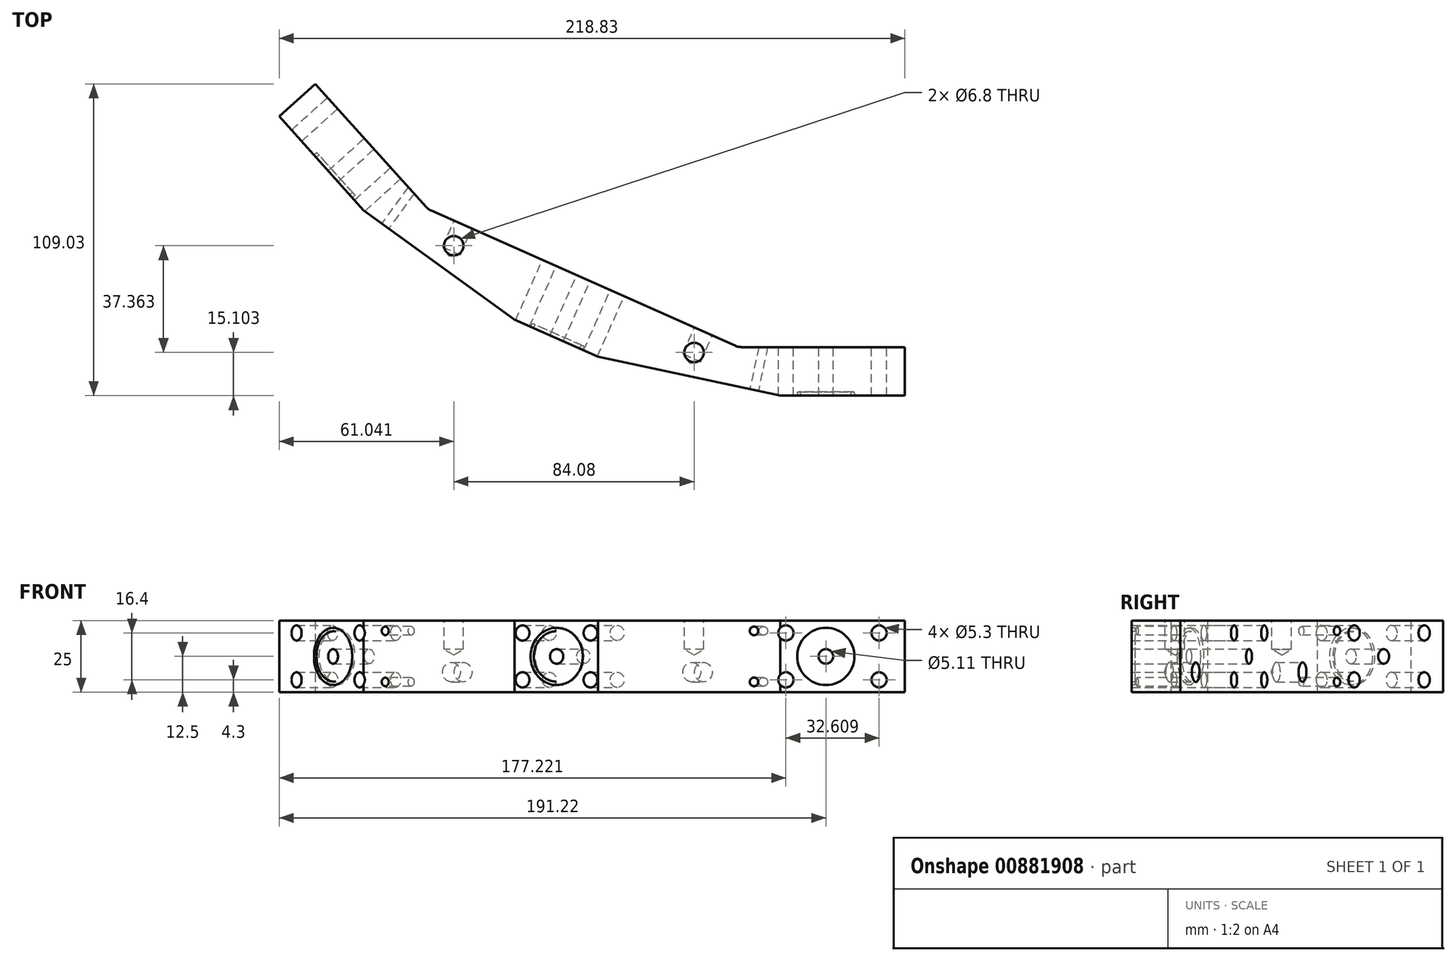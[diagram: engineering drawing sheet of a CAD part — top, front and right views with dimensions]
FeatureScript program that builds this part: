
annotation { "Feature Type Name" : "Feature", "Feature Type Description" : "" }
export const myFeature = defineFeature(function(context is Context, id is Id, definition is map)
    precondition{}
    {
        {
            var Q0;
            Q0=qCreatedBy(makeId("Top.planeOp"),FACE);
            var sketch = newSketch(context, id + "F0", { "sketchPlane" : qUnion([Q0])});
            skCircle(sketch, "E0", {"center": v(0, -260) * mm, "radius": 6 * mm});
            skCircle(sketch, "E1", {"center": v(-105.75, -237.52) * mm, "radius": 6 * mm});
            skCircle(sketch, "E2", {"center": v(-193.22, -173.97) * mm, "radius": 6 * mm});
            skPoint(sketch, "E3", {"position": v(-185.79, -167.28) * mm});
            skPoint(sketch, "E4", {"position": v(-101.68, -228.39) * mm});
            skPoint(sketch, "E5", {"position": v(0, -250) * mm});
            skLineSegment(sketch, "E6.trimOffspring", {"start": v(-103.31, -232.04) * mm, "end": v(-105.75, -237.52) * mm});
            skLineSegment(sketch, "E7.trimOffspring", {"start": v(0, -254) * mm, "end": v(0, -260) * mm});
            skLineSegment(sketch, "E8.trimOffspring", {"start": v(-188.76, -169.96) * mm, "end": v(-193.22, -173.97) * mm});
            skPoint(sketch, "E9", {"position": v(-196.5, -155.4) * mm});
            skPoint(sketch, "E10", {"position": v(-94.36, -211.94) * mm});
            skLineSegment(sketch, "E11", {"start": v(-161.7, -167.13) * mm, "end": v(-108.98, -205.43) * mm});
            skPoint(sketch, "E12", {"position": v(0, -232) * mm});
            skLineSegment(sketch, "E13", {"start": v(0, -232) * mm, "end": v(27.61, -232) * mm});
            skLineSegment(sketch, "E14", {"start": v(0, -232) * mm, "end": v(-16, -232) * mm});
            skLineSegment(sketch, "E15", {"start": v(-79.7, -218.33) * mm, "end": v(-16, -232) * mm});
            skPoint(sketch, "E16.start.orphan", {"position": v(0, 0) * mm});
            skPoint(sketch, "E17.visualSharp", {"position": v(16, -250) * mm});
            skLineSegment(sketch, "E18", {"start": v(-191.22, -134.35) * mm, "end": v(-178.58, -122.97) * mm});
            skLineSegment(sketch, "E19", {"start": v(27.61, -232) * mm, "end": v(27.61, -215) * mm});
            skLineSegment(sketch, "E20", {"start": v(-178.58, -122.97) * mm, "end": v(-149.07, -155.75) * mm});
            skLineSegment(sketch, "E21", {"start": v(-191.22, -134.35) * mm, "end": v(-161.7, -167.13) * mm});
            skLineSegment(sketch, "E22", {"start": v(-16, -215) * mm, "end": v(27.61, -215) * mm});
            skLineSegment(sketch, "E23", {"start": v(-108.98, -205.43) * mm, "end": v(-79.7, -218.33) * mm});
            skLineSegment(sketch, "E24", {"start": v(-125.57, -172.83) * mm, "end": v(-44.45, -208.87) * mm});
            skPoint(sketch, "E25.orphan", {"position": v(-102.07, -189.9) * mm});
            skPoint(sketch, "E26.orphan", {"position": v(-72.9, -202.75) * mm});
            skLineSegment(sketch, "E27", {"start": v(-125.57, -172.83) * mm, "end": v(-138.14, -167.24) * mm});
            skLineSegment(sketch, "E28", {"start": v(-149.07, -155.75) * mm, "end": v(-139.83, -166.02) * mm});
            skLineSegment(sketch, "E29", {"start": v(-44.45, -208.87) * mm, "end": v(-31.64, -214.57) * mm});
            skLineSegment(sketch, "E30", {"start": v(-16, -215) * mm, "end": v(-29.6, -215) * mm});
            skPoint(sketch, "E31.visualSharp", {"position": v(-139.12, -166.8) * mm});
            skArc(sketch, "E31.filletArc", {"start": v(-139.83, -166.02) * mm, "mid": v(-139.05, -166.72) * mm, "end": v(-138.14, -167.24) * mm});
            skPoint(sketch, "E32.visualSharp", {"position": v(-30.67, -215) * mm});
            skArc(sketch, "E32.filletArc", {"start": v(-31.64, -214.57) * mm, "mid": v(-30.65, -214.9) * mm, "end": v(-29.6, -215) * mm});
            skSolve(sketch);
        }
        {
            var Q0;
            Q0=makeQuery(id+"F0.imprint","IMPRINT",FACE,{"disambiguationData":[TD([[makeQuery(id+"F0.imprint","IMPRINT",EDGE,{"derivedFrom":sQuery(id+"F0.wireOp",EDGE,"E11")}),1.0]])]});
            extrude(context, id + "F1", {"entities" : qUnion([Q0]), "depth" : 25 * mm, "offsetDistance" : 25 * mm});
        }
        {
            var Q0;
            Q0=makeQuery(id+"F1.opExtrude","SWEPT_FACE",FACE,{"disambiguationData":[OSD([sQuery(id+"F0.wireOp",EDGE,"E22")])]});
            var sketch = newSketch(context, id + "F2", { "sketchPlane" : qUnion([Q0])});
            skPoint(sketch, "E33", {"position": v(0, 0) * mm});
            skLineSegment(sketch, "E34", {"start": v(0, 0) * mm, "end": v(0, 25) * mm});
            skPoint(sketch, "E35", {"position": v(0, 12.5) * mm});
            skSolve(sketch);
        }
        {
            var Q0;
            Q0=sQuery(id+"F2.wireOp",VERTEX,"E35");
            var Q1;
            Q1=makeQuery(id+"F1.opExtrude","SWEPT_BODY",BODY,{"disambiguationData":[OSD([sQuery(id+"F0.wireOp",EDGE,"E11"),sQuery(id+"F0.wireOp",EDGE,"E13"),sQuery(id+"F0.wireOp",EDGE,"E14"),sQuery(id+"F0.wireOp",EDGE,"E15"),sQuery(id+"F0.wireOp",EDGE,"E18"),sQuery(id+"F0.wireOp",EDGE,"E19"),sQuery(id+"F0.wireOp",EDGE,"E20"),sQuery(id+"F0.wireOp",EDGE,"QAlrF6tD-wXUg-Evcl-dWQj-K1b9825lCyQJ"),sQuery(id+"F0.wireOp",EDGE,"alPorV1Q-hDwH-edkz-XvNq-u1lF4NwrQ3EV"),sQuery(id+"F0.wireOp",EDGE,"E21"),sQuery(id+"F0.wireOp",EDGE,"E22"),sQuery(id+"F0.wireOp",EDGE,"E23"),sQuery(id+"F0.wireOp",EDGE,"E24")])]});
            hole(context, id + "F3", {"style" : HoleStyle.SIMPLE, "endStyle" : HoleEndStyle.THROUGH, "standardTappedOrClearance" : lookupTablePath({ "standard" : "ANSI", "engagement" : "75%", "pitch" : "20 tpi", "size" : "1/4", "type" : "Tapped" }), "standardBlindInLast" : lookupTablePath({ "standard" : "ANSI", "engagement" : "75%", "pitch" : "20 tpi", "size" : "1/4", "type" : "Tapped" }), "holeDiameter" : 5.1 * mm, "majorDiameter" : 6.35 * mm, "showTappedDepth" : true, "isTappedThrough" : true, "tappedDepth" : 7.6 * mm, "tapClearance" : 3, "locations" : qUnion([Q0]), "scope" : qUnion([Q1])});
        }
        {
            var Q0;
            Q0=makeQuery(id+"F1.opExtrude","SWEPT_FACE",FACE,{"disambiguationData":[OSD([sQuery(id+"F0.wireOp",EDGE,"E20")])]});
            var sketch = newSketch(context, id + "F4", { "sketchPlane" : qUnion([Q0])});
            skPoint(sketch, "E36", {"position": v(0, 12.5) * mm});
            skSolve(sketch);
        }
        {
            var Q0;
            Q0=sQuery(id+"F4.wireOp",VERTEX,"E36");
            var Q1;
            Q1=makeQuery(id+"F1.opExtrude","SWEPT_BODY",BODY,{"disambiguationData":[OSD([sQuery(id+"F0.wireOp",EDGE,"E11"),sQuery(id+"F0.wireOp",EDGE,"E13"),sQuery(id+"F0.wireOp",EDGE,"E14"),sQuery(id+"F0.wireOp",EDGE,"E15"),sQuery(id+"F0.wireOp",EDGE,"E18"),sQuery(id+"F0.wireOp",EDGE,"E19"),sQuery(id+"F0.wireOp",EDGE,"E20"),sQuery(id+"F0.wireOp",EDGE,"QAlrF6tD-wXUg-Evcl-dWQj-K1b9825lCyQJ"),sQuery(id+"F0.wireOp",EDGE,"alPorV1Q-hDwH-edkz-XvNq-u1lF4NwrQ3EV"),sQuery(id+"F0.wireOp",EDGE,"E21"),sQuery(id+"F0.wireOp",EDGE,"E22"),sQuery(id+"F0.wireOp",EDGE,"E23"),sQuery(id+"F0.wireOp",EDGE,"E24")])]});
            hole(context, id + "F5", {"style" : HoleStyle.SIMPLE, "endStyle" : HoleEndStyle.THROUGH, "standardTappedOrClearance" : lookupTablePath({ "standard" : "ANSI", "engagement" : "75%", "pitch" : "20 tpi", "size" : "1/4", "type" : "Tapped" }), "standardBlindInLast" : lookupTablePath({ "standard" : "ANSI", "engagement" : "75%", "pitch" : "20 tpi", "size" : "1/4", "type" : "Tapped" }), "holeDiameter" : 5.1 * mm, "majorDiameter" : 6.35 * mm, "showTappedDepth" : true, "isTappedThrough" : true, "tappedDepth" : 7.6 * mm, "tapClearance" : 3, "locations" : qUnion([Q0]), "scope" : qUnion([Q1])});
        }
        {
            var Q0;
            Q0=makeQuery(id+"F1.opExtrude","SWEPT_FACE",FACE,{"disambiguationData":[OSD([sQuery(id+"F0.wireOp",EDGE,"E24")])]});
            var sketch = newSketch(context, id + "F6", { "sketchPlane" : qUnion([Q0])});
            skPoint(sketch, "E37", {"position": v(0, 12.5) * mm});
            skSolve(sketch);
        }
        {
            var Q0;
            Q0=sQuery(id+"F6.wireOp",VERTEX,"E37");
            var Q1;
            Q1=makeQuery(id+"F1.opExtrude","SWEPT_BODY",BODY,{"disambiguationData":[OSD([sQuery(id+"F0.wireOp",EDGE,"E11"),sQuery(id+"F0.wireOp",EDGE,"E13"),sQuery(id+"F0.wireOp",EDGE,"E14"),sQuery(id+"F0.wireOp",EDGE,"E15"),sQuery(id+"F0.wireOp",EDGE,"E18"),sQuery(id+"F0.wireOp",EDGE,"E19"),sQuery(id+"F0.wireOp",EDGE,"E20"),sQuery(id+"F0.wireOp",EDGE,"QAlrF6tD-wXUg-Evcl-dWQj-K1b9825lCyQJ"),sQuery(id+"F0.wireOp",EDGE,"alPorV1Q-hDwH-edkz-XvNq-u1lF4NwrQ3EV"),sQuery(id+"F0.wireOp",EDGE,"E21"),sQuery(id+"F0.wireOp",EDGE,"E22"),sQuery(id+"F0.wireOp",EDGE,"E23"),sQuery(id+"F0.wireOp",EDGE,"E24")])]});
            hole(context, id + "F7", {"style" : HoleStyle.SIMPLE, "endStyle" : HoleEndStyle.THROUGH, "standardTappedOrClearance" : lookupTablePath({ "standard" : "ANSI", "engagement" : "75%", "pitch" : "20 tpi", "size" : "1/4", "type" : "Tapped" }), "standardBlindInLast" : lookupTablePath({ "standard" : "ANSI", "engagement" : "75%", "pitch" : "20 tpi", "size" : "1/4", "type" : "Tapped" }), "holeDiameter" : 5.1 * mm, "majorDiameter" : 6.35 * mm, "showTappedDepth" : true, "isTappedThrough" : true, "tappedDepth" : 7.6 * mm, "tapClearance" : 3, "locations" : qUnion([Q0]), "scope" : qUnion([Q1])});
        }
        {
            var Q0;
            Q0=makeQuery(id+"F1.opExtrude","SWEPT_FACE",FACE,{"disambiguationData":[OSD([sQuery(id+"F0.wireOp",EDGE,"E15")])]});
            var sketch = newSketch(context, id + "F8", { "sketchPlane" : qUnion([Q0])});
            skLineSegment(sketch, "E38", {"start": v(33.02, 25) * mm, "end": v(-32.12, 0) * mm});
            skLineSegment(sketch, "E39", {"start": v(33.02, 0) * mm, "end": v(-32.12, 25) * mm});
            skPoint(sketch, "E40", {"position": v(23.69, 21.42) * mm});
            skPoint(sketch, "E41", {"position": v(23.69, 3.58) * mm});
            skSolve(sketch);
        }
        {
            var Q0;
            Q0=sQuery(id+"F8.wireOp",VERTEX,"E40");
            var Q1;
            Q1=sQuery(id+"F8.wireOp",VERTEX,"E41");
            var Q2;
            Q2=makeQuery(id+"F1.opExtrude","SWEPT_BODY",BODY,{"disambiguationData":[OSD([sQuery(id+"F0.wireOp",EDGE,"E11"),sQuery(id+"F0.wireOp",EDGE,"E13"),sQuery(id+"F0.wireOp",EDGE,"E14"),sQuery(id+"F0.wireOp",EDGE,"E15"),sQuery(id+"F0.wireOp",EDGE,"E18"),sQuery(id+"F0.wireOp",EDGE,"E19"),sQuery(id+"F0.wireOp",EDGE,"E20"),sQuery(id+"F0.wireOp",EDGE,"QAlrF6tD-wXUg-Evcl-dWQj-K1b9825lCyQJ"),sQuery(id+"F0.wireOp",EDGE,"alPorV1Q-hDwH-edkz-XvNq-u1lF4NwrQ3EV"),sQuery(id+"F0.wireOp",EDGE,"E21"),sQuery(id+"F0.wireOp",EDGE,"E22"),sQuery(id+"F0.wireOp",EDGE,"E23"),sQuery(id+"F0.wireOp",EDGE,"E24")])]});
            hole(context, id + "F9", {"style" : HoleStyle.SIMPLE, "endStyle" : HoleEndStyle.THROUGH, "holeDiameter" : 3.02 * mm, "majorDiameter" : 3 * mm, "isTappedThrough" : true, "tappedDepth" : 7.6 * mm, "tapClearance" : 3, "locations" : qUnion([Q0, Q1]), "scope" : qUnion([Q2])});
        }
        {
            var Q0;
            Q0=makeQuery(id+"F1.opExtrude","SWEPT_FACE",FACE,{"disambiguationData":[OSD([sQuery(id+"F0.wireOp",EDGE,"E11")])]});
            var sketch = newSketch(context, id + "F10", { "sketchPlane" : qUnion([Q0])});
            skLineSegment(sketch, "E42", {"start": v(-32.59, 25) * mm, "end": v(32.59, 0) * mm});
            skLineSegment(sketch, "E43", {"start": v(-32.59, 0) * mm, "end": v(32.59, 25) * mm});
            skPoint(sketch, "E44", {"position": v(-23.25, 21.42) * mm});
            skPoint(sketch, "E45", {"position": v(-23.25, 3.58) * mm});
            skSolve(sketch);
        }
        {
            var Q0;
            Q0=sQuery(id+"F10.wireOp",VERTEX,"E44");
            var Q1;
            Q1=sQuery(id+"F10.wireOp",VERTEX,"E45");
            var Q2;
            Q2=makeQuery(id+"F1.opExtrude","SWEPT_BODY",BODY,{"disambiguationData":[OSD([sQuery(id+"F0.wireOp",EDGE,"E11"),sQuery(id+"F0.wireOp",EDGE,"E13"),sQuery(id+"F0.wireOp",EDGE,"E14"),sQuery(id+"F0.wireOp",EDGE,"E15"),sQuery(id+"F0.wireOp",EDGE,"E18"),sQuery(id+"F0.wireOp",EDGE,"E19"),sQuery(id+"F0.wireOp",EDGE,"E20"),sQuery(id+"F0.wireOp",EDGE,"QAlrF6tD-wXUg-Evcl-dWQj-K1b9825lCyQJ"),sQuery(id+"F0.wireOp",EDGE,"alPorV1Q-hDwH-edkz-XvNq-u1lF4NwrQ3EV"),sQuery(id+"F0.wireOp",EDGE,"E21"),sQuery(id+"F0.wireOp",EDGE,"E22"),sQuery(id+"F0.wireOp",EDGE,"E23"),sQuery(id+"F0.wireOp",EDGE,"E24")])]});
            hole(context, id + "F11", {"style" : HoleStyle.SIMPLE, "endStyle" : HoleEndStyle.THROUGH, "holeDiameter" : 3.02 * mm, "majorDiameter" : 5 * mm, "isTappedThrough" : true, "tappedDepth" : 7.6 * mm, "tapClearance" : 3, "locations" : qUnion([Q0, Q1]), "scope" : qUnion([Q2])});
        }
        {
            var Q0;
            Q0=makeQuery(id+"F1.opExtrude","SWEPT_FACE",FACE,{"disambiguationData":[OSD([sQuery(id+"F0.wireOp",EDGE,"E22")])]});
            var sketch = newSketch(context, id + "F12", { "sketchPlane" : qUnion([Q0])});
            skPoint(sketch, "E46", {"position": v(-27.61, 20.7) * mm});
            skPoint(sketch, "E47", {"position": v(-30.61, 20.7) * mm});
            skPoint(sketch, "E48", {"position": v(-27.61, 4.3) * mm});
            skPoint(sketch, "E49", {"position": v(-30.61, 4.3) * mm});
            skPoint(sketch, "E50", {"position": v(-18.61, 20.7) * mm});
            skPoint(sketch, "E51", {"position": v(-18.61, 4.3) * mm});
            skPoint(sketch, "E52", {"position": v(14, 20.7) * mm});
            skPoint(sketch, "E53", {"position": v(14, 4.3) * mm});
            skSolve(sketch);
        }
        {
            var Q0;
            Q0=sQuery(id+"F12.wireOp",VERTEX,"E50");
            var Q1;
            Q1=sQuery(id+"F12.wireOp",VERTEX,"E51");
            var Q2;
            Q2=sQuery(id+"F12.wireOp",VERTEX,"E47");
            var Q3;
            Q3=sQuery(id+"F12.wireOp",VERTEX,"E49");
            var Q4;
            Q4=sQuery(id+"F12.wireOp",VERTEX,"E52");
            var Q5;
            Q5=sQuery(id+"F12.wireOp",VERTEX,"E53");
            var Q6;
            Q6=makeQuery(id+"F1.opExtrude","SWEPT_BODY",BODY,{"disambiguationData":[OSD([sQuery(id+"F0.wireOp",EDGE,"E11"),sQuery(id+"F0.wireOp",EDGE,"E13"),sQuery(id+"F0.wireOp",EDGE,"E14"),sQuery(id+"F0.wireOp",EDGE,"E15"),sQuery(id+"F0.wireOp",EDGE,"E18"),sQuery(id+"F0.wireOp",EDGE,"E19"),sQuery(id+"F0.wireOp",EDGE,"E20"),sQuery(id+"F0.wireOp",EDGE,"QAlrF6tD-wXUg-Evcl-dWQj-K1b9825lCyQJ"),sQuery(id+"F0.wireOp",EDGE,"alPorV1Q-hDwH-edkz-XvNq-u1lF4NwrQ3EV"),sQuery(id+"F0.wireOp",EDGE,"E21"),sQuery(id+"F0.wireOp",EDGE,"E22"),sQuery(id+"F0.wireOp",EDGE,"E23"),sQuery(id+"F0.wireOp",EDGE,"E24")])]});
            hole(context, id + "F13", {"style" : HoleStyle.SIMPLE, "endStyle" : HoleEndStyle.THROUGH, "standardTappedOrClearance" : lookupTablePath({ "fit" : "Close", "standard" : "ISO", "size" : "M5", "type" : "Clearance" }), "standardBlindInLast" : lookupTablePath({ "fit" : "Close", "standard" : "ISO", "size" : "M5", "type" : "Clearance" }), "holeDiameter" : 5.3 * mm, "majorDiameter" : 5 * mm, "isTappedThrough" : true, "tappedDepth" : 7.6 * mm, "tapClearance" : 3, "locations" : qUnion([Q0, Q1, Q2, Q3, Q4, Q5]), "scope" : qUnion([Q6])});
        }
        {
            var Q0;
            Q0=makeQuery(id+"F1.opExtrude","SWEPT_FACE",FACE,{"disambiguationData":[OSD([sQuery(id+"F0.wireOp",EDGE,"E20")])]});
            var sketch = newSketch(context, id + "F14", { "sketchPlane" : qUnion([Q0])});
            skPoint(sketch, "E54", {"position": v(19.1, 20.7) * mm});
            skPoint(sketch, "E55", {"position": v(19.1, 4.3) * mm});
            skPoint(sketch, "E56", {"position": v(-13.85, 20.7) * mm});
            skPoint(sketch, "E57", {"position": v(-13.85, 4.3) * mm});
            skSolve(sketch);
        }
        {
            var Q0;
            Q0=sQuery(id+"F14.wireOp",VERTEX,"fabc1d4e-e931-4de0-b364-7a5eefd0c92b");
            var Q1;
            Q1=sQuery(id+"F14.wireOp",VERTEX,"8a131d87-4429-4834-9a2b-36484b3344fa");
            var Q2;
            Q2=sQuery(id+"F14.wireOp",VERTEX,"E54");
            var Q3;
            Q3=sQuery(id+"F14.wireOp",VERTEX,"E55");
            var Q4;
            Q4=sQuery(id+"F14.wireOp",VERTEX,"E56");
            var Q5;
            Q5=sQuery(id+"F14.wireOp",VERTEX,"E57");
            var Q6;
            Q6=makeQuery(id+"F1.opExtrude","SWEPT_BODY",BODY,{"disambiguationData":[OSD([sQuery(id+"F0.wireOp",EDGE,"E11"),sQuery(id+"F0.wireOp",EDGE,"E13"),sQuery(id+"F0.wireOp",EDGE,"E14"),sQuery(id+"F0.wireOp",EDGE,"E15"),sQuery(id+"F0.wireOp",EDGE,"E18"),sQuery(id+"F0.wireOp",EDGE,"E19"),sQuery(id+"F0.wireOp",EDGE,"E20"),sQuery(id+"F0.wireOp",EDGE,"QAlrF6tD-wXUg-Evcl-dWQj-K1b9825lCyQJ"),sQuery(id+"F0.wireOp",EDGE,"alPorV1Q-hDwH-edkz-XvNq-u1lF4NwrQ3EV"),sQuery(id+"F0.wireOp",EDGE,"E21"),sQuery(id+"F0.wireOp",EDGE,"E22"),sQuery(id+"F0.wireOp",EDGE,"E23"),sQuery(id+"F0.wireOp",EDGE,"E24")])]});
            hole(context, id + "F15", {"style" : HoleStyle.SIMPLE, "endStyle" : HoleEndStyle.THROUGH, "standardTappedOrClearance" : lookupTablePath({ "fit" : "Close", "standard" : "ISO", "size" : "M5", "type" : "Clearance" }), "standardBlindInLast" : lookupTablePath({ "fit" : "Close", "standard" : "ISO", "size" : "M5", "type" : "Clearance" }), "holeDiameter" : 5.3 * mm, "majorDiameter" : 5 * mm, "isTappedThrough" : true, "tappedDepth" : 7.6 * mm, "tapClearance" : 3, "locations" : qUnion([Q0, Q1, Q2, Q3, Q4, Q5]), "scope" : qUnion([Q6])});
        }
        {
            var Q0;
            Q0=makeQuery(id+"F1.opExtrude","SWEPT_FACE",FACE,{"disambiguationData":[OSD([sQuery(id+"F0.wireOp",EDGE,"E24")])]});
            var sketch = newSketch(context, id + "F16", { "sketchPlane" : qUnion([Q0])});
            skPoint(sketch, "E58", {"position": v(13.05, 20.7) * mm});
            skPoint(sketch, "E59", {"position": v(13.05, 4.3) * mm});
            skPoint(sketch, "E60", {"position": v(-12.95, 20.7) * mm});
            skPoint(sketch, "E61", {"position": v(-12.95, 4.3) * mm});
            skSolve(sketch);
        }
        {
            var Q0;
            Q0=sQuery(id+"F16.wireOp",VERTEX,"E60");
            var Q1;
            Q1=sQuery(id+"F16.wireOp",VERTEX,"E58");
            var Q2;
            Q2=sQuery(id+"F16.wireOp",VERTEX,"E59");
            var Q3;
            Q3=sQuery(id+"F16.wireOp",VERTEX,"E61");
            var Q4;
            Q4=makeQuery(id+"F1.opExtrude","SWEPT_BODY",BODY,{"disambiguationData":[OSD([sQuery(id+"F0.wireOp",EDGE,"E11"),sQuery(id+"F0.wireOp",EDGE,"E13"),sQuery(id+"F0.wireOp",EDGE,"E14"),sQuery(id+"F0.wireOp",EDGE,"E15"),sQuery(id+"F0.wireOp",EDGE,"E18"),sQuery(id+"F0.wireOp",EDGE,"E19"),sQuery(id+"F0.wireOp",EDGE,"E20"),sQuery(id+"F0.wireOp",EDGE,"QAlrF6tD-wXUg-Evcl-dWQj-K1b9825lCyQJ"),sQuery(id+"F0.wireOp",EDGE,"alPorV1Q-hDwH-edkz-XvNq-u1lF4NwrQ3EV"),sQuery(id+"F0.wireOp",EDGE,"E21"),sQuery(id+"F0.wireOp",EDGE,"E22"),sQuery(id+"F0.wireOp",EDGE,"E23"),sQuery(id+"F0.wireOp",EDGE,"E24")])]});
            hole(context, id + "F17", {"style" : HoleStyle.SIMPLE, "endStyle" : HoleEndStyle.THROUGH, "standardTappedOrClearance" : lookupTablePath({ "fit" : "Close", "standard" : "ISO", "size" : "M5", "type" : "Clearance" }), "standardBlindInLast" : lookupTablePath({ "fit" : "Close", "standard" : "ISO", "size" : "M5", "type" : "Clearance" }), "holeDiameter" : 5.3 * mm, "majorDiameter" : 5 * mm, "isTappedThrough" : true, "tappedDepth" : 7.6 * mm, "tapClearance" : 3, "locations" : qUnion([Q0, Q1, Q2, Q3]), "scope" : qUnion([Q4])});
        }
        {
            var Q0;
            Q0=makeQuery(id+"F1.opExtrude","SWEPT_FACE",FACE,{"disambiguationData":[OSD([sQuery(id+"F0.wireOp",EDGE,"E21")])]});
            var sketch = newSketch(context, id + "F18", { "sketchPlane" : qUnion([Q0])});
            skPoint(sketch, "E62", {"position": v(0, 12.5) * mm});
            skCircle(sketch, "E63", {"center": v(0, 12.5) * mm, "radius": 10 * mm});
            skCircle(sketch, "E64", {"center": v(0, 12.5) * mm, "radius": 8.8 * mm});
            skSolve(sketch);
        }
        {
            var Q0;
            Q0=makeQuery(id+"F18.imprint","IMPRINT",FACE,{"disambiguationData":[TD([[makeQuery(id+"F18.imprint","IMPRINT",EDGE,{"derivedFrom":sQuery(id+"F18.wireOp",EDGE,"E63")}),1.0]])]});
            extrude(context, id + "F19", {"entities" : qUnion([Q0]), "operationType" : NewBodyOperationType.REMOVE, "oppositeDirection" : true, "depth" : 1.3 * mm, "offsetDistance" : 25 * mm, "hasDraft" : true, "draftAngle" : 2 * degree});
        }
        {
            var Q0;
            Q0=makeQuery(id+"F19.boolean.opBoolean","COPY",EDGE,{"derivedFrom":makeQuery(id+"F19.opExtrude","CAP_EDGE",EDGE,{"disambiguationData":[OSD([sQuery(id+"F18.wireOp",EDGE,"E63")])],"isStart":true})});
            var Q1;
            Q1=makeQuery(id+"F19.boolean.opBoolean","COPY",EDGE,{"derivedFrom":makeQuery(id+"F19.opExtrude","CAP_EDGE",EDGE,{"disambiguationData":[OSD([sQuery(id+"F18.wireOp",EDGE,"E63")])],"isStart":false})});
            fillet(context, id + "F20", {"entities" : qUnion([Q0, Q1]), "radius" : 0.2 * mm, "tangentPropagation" : true, "allowEdgeOverflow" : false});
        }
        {
            var Q0;
            Q0=makeQuery(id+"F19.boolean.opBoolean","COPY",EDGE,{"derivedFrom":makeQuery(id+"F19.opExtrude","CAP_EDGE",EDGE,{"disambiguationData":[OSD([sQuery(id+"F18.wireOp",EDGE,"E64")])],"isStart":true})});
            fillet(context, id + "F21", {"entities" : qUnion([Q0]), "radius" : 0.2 * mm, "tangentPropagation" : true, "allowEdgeOverflow" : false});
        }
        {
            var Q0;
            Q0=makeQuery(id+"F1.opExtrude","SWEPT_FACE",FACE,{"disambiguationData":[OSD([sQuery(id+"F0.wireOp",EDGE,"E23")])]});
            var sketch = newSketch(context, id + "F22", { "sketchPlane" : qUnion([Q0])});
            skLineSegment(sketch, "E65", {"start": v(-0.75, 12.5) * mm, "end": v(-0.92, 25) * mm});
            skCircle(sketch, "E66", {"center": v(-0.75, 12.5) * mm, "radius": 10 * mm});
            skCircle(sketch, "E67", {"center": v(-0.75, 12.5) * mm, "radius": 8.8 * mm});
            skSolve(sketch);
        }
        {
            var Q0;
            Q0=makeQuery(id+"F22.imprint","IMPRINT",FACE,{"disambiguationData":[TD([[makeQuery(id+"F22.imprint","IMPRINT",EDGE,{"derivedFrom":sQuery(id+"F22.wireOp",EDGE,"E66")}),1.0]])]});
            extrude(context, id + "F23", {"entities" : qUnion([Q0]), "operationType" : NewBodyOperationType.REMOVE, "oppositeDirection" : true, "depth" : 1.3 * mm, "offsetDistance" : 25 * mm, "hasDraft" : true, "draftAngle" : 2 * degree, "draftPullDirection" : true});
        }
        {
            var Q0;
            Q0=makeQuery(id+"F23.boolean.opBoolean","COPY",EDGE,{"derivedFrom":makeQuery(id+"F23.opExtrude","CAP_EDGE",EDGE,{"disambiguationData":[OSD([sQuery(id+"F22.wireOp",EDGE,"E66")])],"isStart":true})});
            var Q1;
            Q1=makeQuery(id+"F23.boolean.opBoolean","COPY",EDGE,{"derivedFrom":makeQuery(id+"F23.opExtrude","CAP_EDGE",EDGE,{"disambiguationData":[OSD([sQuery(id+"F22.wireOp",EDGE,"E67")])],"isStart":true})});
            var Q2;
            Q2=makeQuery(id+"F23.boolean.opBoolean","COPY",EDGE,{"derivedFrom":makeQuery(id+"F23.opExtrude","CAP_EDGE",EDGE,{"disambiguationData":[OSD([sQuery(id+"F22.wireOp",EDGE,"E66")])],"isStart":false})});
            fillet(context, id + "F24", {"entities" : qUnion([Q0, Q1, Q2]), "radius" : 0.2 * mm, "tangentPropagation" : true, "allowEdgeOverflow" : false});
        }
        {
            var Q0;
            Q0=makeQuery(id+"F1.opExtrude","SWEPT_FACE",FACE,{"disambiguationData":[OSD([sQuery(id+"F0.wireOp",EDGE,"E13"),sQuery(id+"F0.wireOp",EDGE,"E14")])]});
            var sketch = newSketch(context, id + "F25", { "sketchPlane" : qUnion([Q0])});
            skCircle(sketch, "E68", {"center": v(0, 12.5) * mm, "radius": 10 * mm});
            skCircle(sketch, "E69", {"center": v(0, 12.5) * mm, "radius": 8.8 * mm});
            skSolve(sketch);
        }
        {
            var Q0;
            Q0=makeQuery(id+"F25.imprint","IMPRINT",FACE,{"disambiguationData":[TD([[makeQuery(id+"F25.imprint","IMPRINT",EDGE,{"derivedFrom":sQuery(id+"F25.wireOp",EDGE,"E68")}),1.0]])]});
            extrude(context, id + "F26", {"entities" : qUnion([Q0]), "operationType" : NewBodyOperationType.REMOVE, "oppositeDirection" : true, "depth" : 1.3 * mm, "offsetDistance" : 25 * mm, "hasDraft" : true, "draftAngle" : 2 * degree, "draftPullDirection" : true});
        }
        {
            var Q0;
            Q0=makeQuery(id+"F26.boolean.opBoolean","COPY",EDGE,{"derivedFrom":makeQuery(id+"F26.opExtrude","CAP_EDGE",EDGE,{"disambiguationData":[OSD([sQuery(id+"F25.wireOp",EDGE,"E68")])],"isStart":true})});
            var Q1;
            Q1=makeQuery(id+"F26.boolean.opBoolean","COPY",EDGE,{"derivedFrom":makeQuery(id+"F26.opExtrude","CAP_EDGE",EDGE,{"disambiguationData":[OSD([sQuery(id+"F25.wireOp",EDGE,"E68")])],"isStart":false})});
            fillet(context, id + "F27", {"entities" : qUnion([Q0, Q1]), "radius" : 0.2 * mm, "tangentPropagation" : true, "allowEdgeOverflow" : false});
        }
        {
            var Q0;
            Q0=makeQuery(id+"F26.boolean.opBoolean","COPY",EDGE,{"derivedFrom":makeQuery(id+"F26.opExtrude","CAP_EDGE",EDGE,{"disambiguationData":[OSD([sQuery(id+"F25.wireOp",EDGE,"E69")])],"isStart":true})});
            var Q1;
            Q1=makeQuery(id+"F26.boolean.opBoolean","COPY",EDGE,{"derivedFrom":makeQuery(id+"F26.opExtrude","CAP_EDGE",EDGE,{"disambiguationData":[OSD([sQuery(id+"F25.wireOp",EDGE,"E69")])],"isStart":false})});
            fillet(context, id + "F28", {"entities" : qUnion([Q0, Q1]), "radius" : 0.2 * mm, "tangentPropagation" : true, "allowEdgeOverflow" : false});
        }
        {
            var Q0;
            Q0=makeQuery(id+"F23.boolean.opBoolean","COPY",EDGE,{"derivedFrom":makeQuery(id+"F23.opExtrude","CAP_EDGE",EDGE,{"disambiguationData":[OSD([sQuery(id+"F22.wireOp",EDGE,"E67")])],"isStart":false})});
            fillet(context, id + "F29", {"entities" : qUnion([Q0]), "radius" : 0.2 * mm, "tangentPropagation" : true, "allowEdgeOverflow" : false});
        }
        {
            var Q0;
            Q0=makeQuery(id+"F19.boolean.opBoolean","COPY",EDGE,{"derivedFrom":makeQuery(id+"F19.opExtrude","CAP_EDGE",EDGE,{"disambiguationData":[OSD([sQuery(id+"F18.wireOp",EDGE,"E64")])],"isStart":false})});
            fillet(context, id + "F30", {"entities" : qUnion([Q0]), "radius" : 0.2 * mm, "tangentPropagation" : true, "allowEdgeOverflow" : false});
        }
        {
            var Q0;
            Q0=makeQuery(id+"F1.opExtrude","SWEPT_FACE",FACE,{"disambiguationData":[OSD([sQuery(id+"F0.wireOp",EDGE,"E24"),sQuery(id+"F0.wireOp",EDGE,"E27"),sQuery(id+"F0.wireOp",EDGE,"E29")])]});
            var sketch = newSketch(context, id + "F31", { "sketchPlane" : qUnion([Q0])});
            skPoint(sketch, "E70", {"position": v(46.05, 7) * mm});
            skPoint(sketch, "E71", {"position": v(-45.95, 7) * mm});
            skLineSegment(sketch, "E72", {"start": v(-58.22, 0) * mm, "end": v(58.33, 0) * mm});
            skLineSegment(sketch, "E73", {"start": v(-45.95, 7) * mm, "end": v(-58.22, 7) * mm});
            skPoint(sketch, "E73.endSnap0", {"position": v(-58.22, 12.5) * mm});
            skLineSegment(sketch, "E74", {"start": v(46.05, 7) * mm, "end": v(58.33, 7) * mm});
            skSolve(sketch);
        }
        {
            var Q0;
            Q0=sQuery(id+"F31.wireOp",VERTEX,"c76b1e38-4467-41f2-b8a1-92f386a41068");
            var Q1;
            Q1=sQuery(id+"F31.wireOp",VERTEX,"34d30ba8-ade5-4ee9-ae17-0df2fffb3929");
            var Q2;
            Q2=sQuery(id+"F31.wireOp",VERTEX,"ed0e6a08-3dcf-44a9-ac8f-dfb5b3668196");
            var Q3;
            Q3=sQuery(id+"F31.wireOp",VERTEX,"E70");
            var Q4;
            Q4=sQuery(id+"F31.wireOp",VERTEX,"E71");
            var Q5;
            Q5=makeQuery(id+"F1.opExtrude","SWEPT_BODY",BODY,{"disambiguationData":[OSD([sQuery(id+"F0.wireOp",EDGE,"E11"),sQuery(id+"F0.wireOp",EDGE,"E13"),sQuery(id+"F0.wireOp",EDGE,"E14"),sQuery(id+"F0.wireOp",EDGE,"E15"),sQuery(id+"F0.wireOp",EDGE,"E18"),sQuery(id+"F0.wireOp",EDGE,"E19"),sQuery(id+"F0.wireOp",EDGE,"E20"),sQuery(id+"F0.wireOp",EDGE,"E21"),sQuery(id+"F0.wireOp",EDGE,"E22"),sQuery(id+"F0.wireOp",EDGE,"E23"),sQuery(id+"F0.wireOp",EDGE,"E24"),sQuery(id+"F0.wireOp",EDGE,"E27"),sQuery(id+"F0.wireOp",EDGE,"E28"),sQuery(id+"F0.wireOp",EDGE,"E29"),sQuery(id+"F0.wireOp",EDGE,"E30"),sQuery(id+"F0.wireOp",EDGE,"E31.filletArc"),sQuery(id+"F0.wireOp",EDGE,"E32.filletArc")])]});
            hole(context, id + "F32", {"style" : HoleStyle.SIMPLE, "endStyle" : HoleEndStyle.BLIND, "standardTappedOrClearance" : lookupTablePath({ "standard" : "ISO", "engagement" : "75%", "pitch" : "1.25 mm", "size" : "M8", "type" : "Tapped" }), "standardBlindInLast" : lookupTablePath({ "standard" : "ISO", "engagement" : "75%", "pitch" : "1.25 mm", "size" : "M8", "type" : "Tapped" }), "holeDiameter" : 6.8 * mm, "majorDiameter" : 8 * mm, "showTappedDepth" : true, "holeDepth" : 10 * mm, "isTappedThrough" : true, "tappedDepth" : 6.25 * mm, "tapClearance" : 3, "locations" : qUnion([Q0, Q1, Q2, Q3, Q4]), "scope" : qUnion([Q5])});
        }
        {
            var Q0;
            Q0=makeQuery(id+"F1.opExtrude","CAP_FACE",FACE,{"disambiguationData":[OSD([sQuery(id+"F0.wireOp",EDGE,"E11"),sQuery(id+"F0.wireOp",EDGE,"E13"),sQuery(id+"F0.wireOp",EDGE,"E14"),sQuery(id+"F0.wireOp",EDGE,"E15"),sQuery(id+"F0.wireOp",EDGE,"E18"),sQuery(id+"F0.wireOp",EDGE,"E19"),sQuery(id+"F0.wireOp",EDGE,"E20"),sQuery(id+"F0.wireOp",EDGE,"E21"),sQuery(id+"F0.wireOp",EDGE,"E22"),sQuery(id+"F0.wireOp",EDGE,"E23"),sQuery(id+"F0.wireOp",EDGE,"E24"),sQuery(id+"F0.wireOp",EDGE,"E27"),sQuery(id+"F0.wireOp",EDGE,"E28"),sQuery(id+"F0.wireOp",EDGE,"E29"),sQuery(id+"F0.wireOp",EDGE,"E30"),sQuery(id+"F0.wireOp",EDGE,"E31.filletArc"),sQuery(id+"F0.wireOp",EDGE,"E32.filletArc")])],"isStart":false});
            var sketch = newSketch(context, id + "F33", { "sketchPlane" : qUnion([Q0])});
            skPoint(sketch, "E75", {"position": v(-42.85, -209.59) * mm});
            skPoint(sketch, "E76", {"position": v(-126.93, -172.22) * mm});
            skLineSegment(sketch, "E77", {"start": v(-42.85, -209.59) * mm, "end": v(-46.1, -216.9) * mm});
            skLineSegment(sketch, "E78", {"start": v(-126.93, -172.22) * mm, "end": v(-130.18, -179.53) * mm});
            skPoint(sketch, "E79", {"position": v(-46.1, -216.9) * mm});
            skPoint(sketch, "E80", {"position": v(-130.18, -179.53) * mm});
            skLineSegment(sketch, "E81", {"start": v(-46.1, -216.9) * mm, "end": v(-49.6, -224.79) * mm, "construction": true});
            skSolve(sketch);
        }
        {
            var Q0;
            Q0=sQuery(id+"F33.wireOp",VERTEX,"E79");
            var Q1;
            Q1=sQuery(id+"F33.wireOp",VERTEX,"E78.end");
            var Q2;
            Q2=makeQuery(id+"F1.opExtrude","SWEPT_BODY",BODY,{"disambiguationData":[OSD([sQuery(id+"F0.wireOp",EDGE,"E11"),sQuery(id+"F0.wireOp",EDGE,"E13"),sQuery(id+"F0.wireOp",EDGE,"E14"),sQuery(id+"F0.wireOp",EDGE,"E15"),sQuery(id+"F0.wireOp",EDGE,"E18"),sQuery(id+"F0.wireOp",EDGE,"E19"),sQuery(id+"F0.wireOp",EDGE,"E20"),sQuery(id+"F0.wireOp",EDGE,"E21"),sQuery(id+"F0.wireOp",EDGE,"E22"),sQuery(id+"F0.wireOp",EDGE,"E23"),sQuery(id+"F0.wireOp",EDGE,"E24"),sQuery(id+"F0.wireOp",EDGE,"E27"),sQuery(id+"F0.wireOp",EDGE,"E28"),sQuery(id+"F0.wireOp",EDGE,"E29"),sQuery(id+"F0.wireOp",EDGE,"E30"),sQuery(id+"F0.wireOp",EDGE,"E31.filletArc"),sQuery(id+"F0.wireOp",EDGE,"E32.filletArc")])]});
            hole(context, id + "F34", {"style" : HoleStyle.SIMPLE, "endStyle" : HoleEndStyle.BLIND, "standardTappedOrClearance" : lookupTablePath({ "standard" : "ISO", "engagement" : "75%", "pitch" : "1.25 mm", "size" : "M8", "type" : "Tapped" }), "standardBlindInLast" : lookupTablePath({ "standard" : "ISO", "engagement" : "75%", "pitch" : "1.25 mm", "size" : "M8", "type" : "Tapped" }), "holeDiameter" : 6.8 * mm, "majorDiameter" : 8 * mm, "showTappedDepth" : true, "holeDepth" : 10 * mm, "isTappedThrough" : true, "tappedDepth" : 6.25 * mm, "tapClearance" : 3, "locations" : qUnion([Q0, Q1]), "scope" : qUnion([Q2])});
        }
    });
